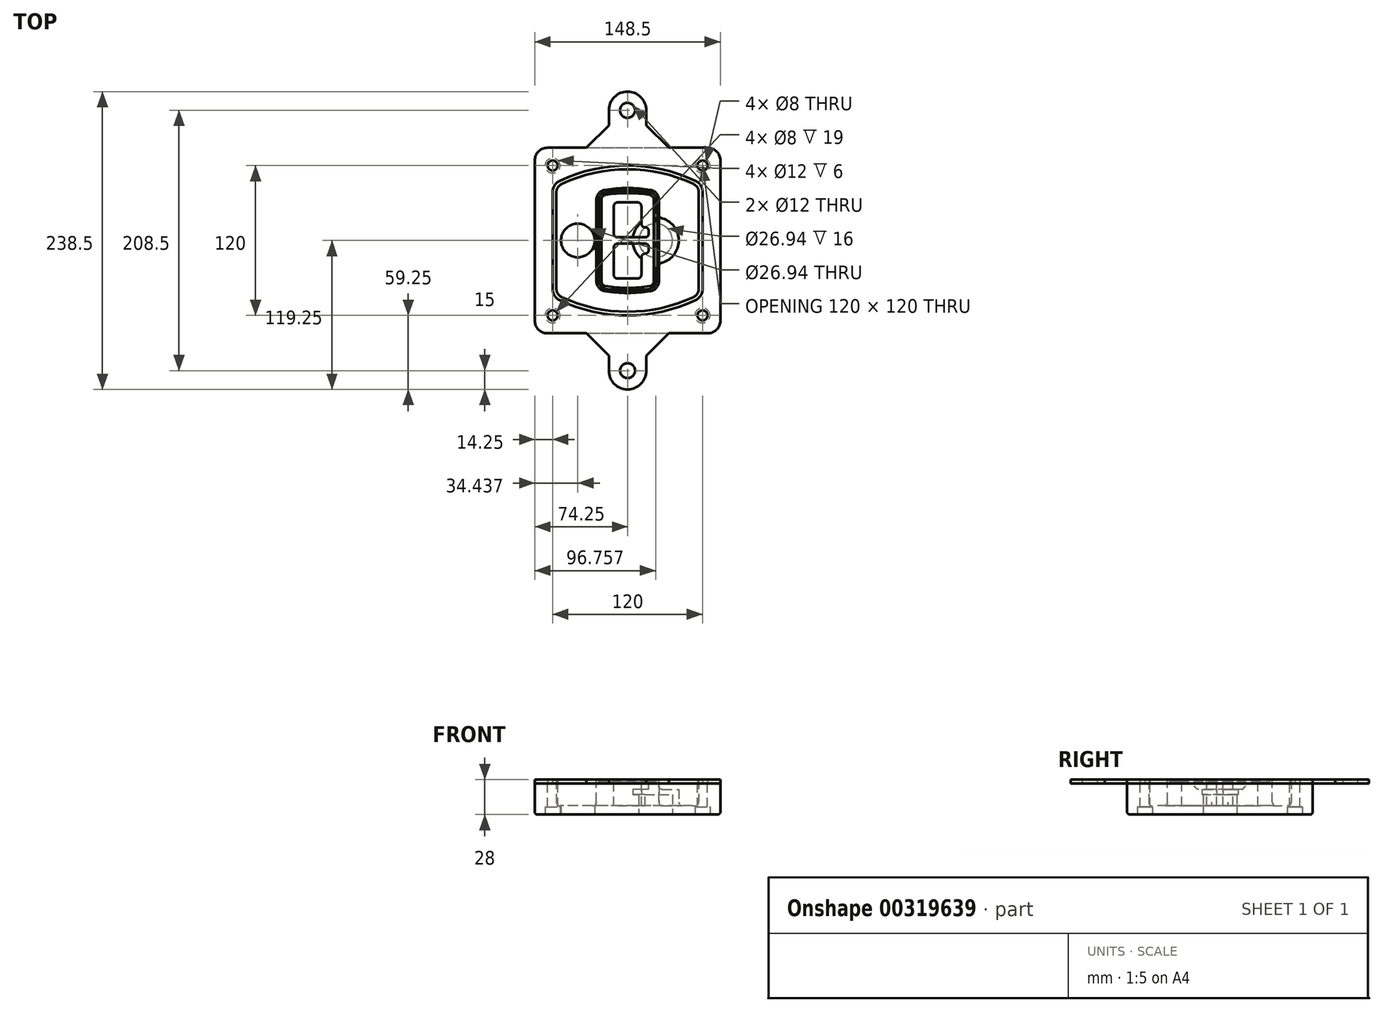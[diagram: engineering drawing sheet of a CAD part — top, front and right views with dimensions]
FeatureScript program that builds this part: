
annotation { "Feature Type Name" : "Feature", "Feature Type Description" : "" }
export const myFeature = defineFeature(function(context is Context, id is Id, definition is map)
    precondition{}
    {
        {
            var Q0;
            Q0=qCreatedBy(makeId("Top.planeOp"),FACE);
            var sketch = newSketch(context, id + "F0", { "sketchPlane" : qUnion([Q0])});
            skPoint(sketch, "E0.rect.middle", {"position": v(0, 0) * mm});
            skLineSegment(sketch, "E1.bottom", {"start": v(-64.25, -74.25) * mm, "end": v(64.25, -74.25) * mm});
            skLineSegment(sketch, "E1.top", {"start": v(-64.25, 74.25) * mm, "end": v(64.25, 74.25) * mm});
            skLineSegment(sketch, "E1.left", {"start": v(-74.25, -64.25) * mm, "end": v(-74.25, 64.25) * mm});
            skLineSegment(sketch, "E1.right", {"start": v(74.25, -64.25) * mm, "end": v(74.25, 64.25) * mm});
            skLineSegment(sketch, "E2", {"start": v(-74.25, 74.25) * mm, "end": v(74.25, -74.25) * mm, "construction": true});
            skLineSegment(sketch, "E3", {"start": v(74.25, 74.25) * mm, "end": v(-74.25, -74.25) * mm, "construction": true});
            skCircle(sketch, "E4", {"center": v(-60, 60) * mm, "radius": 4 * mm});
            skCircle(sketch, "E5", {"center": v(60, 60) * mm, "radius": 4 * mm});
            skCircle(sketch, "E6", {"center": v(60, -60) * mm, "radius": 4 * mm});
            skCircle(sketch, "E7", {"center": v(-60, -60) * mm, "radius": 4 * mm});
            skLineSegment(sketch, "E8", {"start": v(-60, 60) * mm, "end": v(60, 60) * mm, "construction": true});
            skLineSegment(sketch, "E9", {"start": v(60, 60) * mm, "end": v(60, -60) * mm, "construction": true});
            skLineSegment(sketch, "E10", {"start": v(60, -60) * mm, "end": v(-60, -60) * mm, "construction": true});
            skLineSegment(sketch, "E11", {"start": v(-60, -60) * mm, "end": v(-60, 60) * mm, "construction": true});
            skLineSegment(sketch, "E12", {"start": v(-60, 38.83) * mm, "end": v(-60, -38.83) * mm});
            skLineSegment(sketch, "E13", {"start": v(60, 38.83) * mm, "end": v(60, -38.83) * mm});
            skArc(sketch, "E14", {"start": v(54.26, 47.88) * mm, "mid": v(0, 60) * mm, "end": v(-54.26, 47.88) * mm});
            skArc(sketch, "E15", {"start": v(-54.26, -47.88) * mm, "mid": v(0, -60) * mm, "end": v(54.26, -47.88) * mm});
            skLineSegment(sketch, "E16", {"start": v(-60, 0) * mm, "end": v(60, 0) * mm, "construction": true});
            skPoint(sketch, "E17.visualSharp", {"position": v(-60, -45) * mm});
            skArc(sketch, "E17.filletArc", {"start": v(-60, -38.83) * mm, "mid": v(-58.44, -44.2) * mm, "end": v(-54.26, -47.88) * mm});
            skPoint(sketch, "E18.visualSharp", {"position": v(-60, 45) * mm});
            skArc(sketch, "E18.filletArc", {"start": v(-54.26, 47.88) * mm, "mid": v(-58.44, 44.2) * mm, "end": v(-60, 38.83) * mm});
            skPoint(sketch, "E19.visualSharp", {"position": v(60, 45) * mm});
            skArc(sketch, "E19.filletArc", {"start": v(60, 38.83) * mm, "mid": v(58.44, 44.2) * mm, "end": v(54.26, 47.88) * mm});
            skPoint(sketch, "E20.visualSharp", {"position": v(60, -45) * mm});
            skArc(sketch, "E20.filletArc", {"start": v(54.26, -47.88) * mm, "mid": v(58.44, -44.2) * mm, "end": v(60, -38.83) * mm});
            skPoint(sketch, "E21.visualSharp", {"position": v(-74.25, 74.25) * mm});
            skArc(sketch, "E21.filletArc", {"start": v(-64.25, 74.25) * mm, "mid": v(-71.32, 71.32) * mm, "end": v(-74.25, 64.25) * mm});
            skPoint(sketch, "E22.visualSharp", {"position": v(74.25, 74.25) * mm});
            skArc(sketch, "E22.filletArc", {"start": v(74.25, 64.25) * mm, "mid": v(71.32, 71.32) * mm, "end": v(64.25, 74.25) * mm});
            skPoint(sketch, "E23.visualSharp", {"position": v(74.25, -74.25) * mm});
            skArc(sketch, "E23.filletArc", {"start": v(64.25, -74.25) * mm, "mid": v(71.32, -71.32) * mm, "end": v(74.25, -64.25) * mm});
            skPoint(sketch, "E24.visualSharp", {"position": v(-74.25, -74.25) * mm});
            skArc(sketch, "E24.filletArc", {"start": v(-74.25, -64.25) * mm, "mid": v(-71.32, -71.32) * mm, "end": v(-64.25, -74.25) * mm});
            skArc(sketch, "E25.0", {"start": v(57, 38.83) * mm, "mid": v(55.9, 42.58) * mm, "end": v(52.98, 45.17) * mm});
            skLineSegment(sketch, "E25.1", {"start": v(57, 38.83) * mm, "end": v(57, -38.83) * mm});
            skArc(sketch, "E25.2", {"start": v(52.98, -45.17) * mm, "mid": v(55.9, -42.58) * mm, "end": v(57, -38.83) * mm});
            skArc(sketch, "E25.3", {"start": v(-52.98, -45.17) * mm, "mid": v(0, -57) * mm, "end": v(52.98, -45.17) * mm});
            skArc(sketch, "E25.4", {"start": v(-57, -38.83) * mm, "mid": v(-55.9, -42.58) * mm, "end": v(-52.98, -45.17) * mm});
            skArc(sketch, "E25.5", {"start": v(52.98, 45.17) * mm, "mid": v(0, 57) * mm, "end": v(-52.98, 45.17) * mm});
            skLineSegment(sketch, "E25.6", {"start": v(-57, 38.83) * mm, "end": v(-57, -38.83) * mm});
            skArc(sketch, "E25.7", {"start": v(-52.98, 45.17) * mm, "mid": v(-55.9, 42.58) * mm, "end": v(-57, 38.83) * mm});
            skArc(sketch, "E26.0", {"start": v(-55.96, 51.5) * mm, "mid": v(-61.82, 46.33) * mm, "end": v(-64, 38.83) * mm});
            skArc(sketch, "E26.1", {"start": v(55.96, 51.5) * mm, "mid": v(0, 64) * mm, "end": v(-55.96, 51.5) * mm});
            skArc(sketch, "E26.2", {"start": v(64, 38.83) * mm, "mid": v(61.82, 46.33) * mm, "end": v(55.96, 51.5) * mm});
            skLineSegment(sketch, "E26.3", {"start": v(64, 38.83) * mm, "end": v(64, -38.83) * mm});
            skArc(sketch, "E26.4", {"start": v(55.96, -51.5) * mm, "mid": v(61.82, -46.33) * mm, "end": v(64, -38.83) * mm});
            skLineSegment(sketch, "E26.5", {"start": v(-64, 38.83) * mm, "end": v(-64, -38.83) * mm});
            skArc(sketch, "E26.6", {"start": v(-55.96, -51.5) * mm, "mid": v(0, -64) * mm, "end": v(55.96, -51.5) * mm});
            skArc(sketch, "E26.7", {"start": v(-64, -38.83) * mm, "mid": v(-61.82, -46.33) * mm, "end": v(-55.96, -51.5) * mm});
            skSolve(sketch);
        }
        {
            var Q0;
            Q0=makeQuery(id+"F0.imprint","IMPRINT",FACE,{"disambiguationData":[TD([[makeQuery(id+"F0.imprint","IMPRINT",EDGE,{"derivedFrom":sQuery(id+"F0.wireOp",EDGE,"E1.bottom")}),1.0]])]});
            var Q1;
            Q1=makeQuery(id+"F0.imprint","IMPRINT",FACE,{"disambiguationData":[TD([[makeQuery(id+"F0.imprint","IMPRINT",EDGE,{"derivedFrom":sQuery(id+"F0.wireOp",EDGE,"E12")}),1.0]])]});
            var Q2;
            Q2=makeQuery(id+"F0.imprint","IMPRINT",FACE,{"disambiguationData":[TD([[makeQuery(id+"F0.imprint","IMPRINT",EDGE,{"derivedFrom":sQuery(id+"F0.wireOp",EDGE,"E25.0")}),1.0]])]});
            var Q3;
            Q3=makeQuery(id+"F0.imprint","IMPRINT",FACE,{"disambiguationData":[TD([[makeQuery(id+"F0.imprint","IMPRINT",EDGE,{"derivedFrom":sQuery(id+"F0.wireOp",EDGE,"E12")}),-1.0]])]});
            extrude(context, id + "F1", {"entities" : qUnion([Q0, Q1, Q2, Q3]), "oppositeDirection" : true, "depth" : 25 * mm});
        }
        {
            var Q0;
            Q0=makeQuery(id+"F0.imprint","IMPRINT",FACE,{"disambiguationData":[TD([[makeQuery(id+"F0.imprint","IMPRINT",EDGE,{"derivedFrom":sQuery(id+"F0.wireOp",EDGE,"E12")}),1.0]])]});
            extrude(context, id + "F2", {"entities" : qUnion([Q0]), "operationType" : NewBodyOperationType.ADD, "depth" : 3 * mm});
        }
        {
            var Q0;
            Q0=makeQuery(id+"F0.imprint","IMPRINT",FACE,{"disambiguationData":[TD([[makeQuery(id+"F0.imprint","IMPRINT",EDGE,{"derivedFrom":sQuery(id+"F0.wireOp",EDGE,"E25.0")}),1.0]])]});
            extrude(context, id + "F3", {"entities" : qUnion([Q0]), "operationType" : NewBodyOperationType.REMOVE, "oppositeDirection" : true, "depth" : 18 * mm});
        }
        {
            var Q0;
            Q0=makeQuery(id+"F2.opExtrude","CAP_FACE",FACE,{"disambiguationData":[OSD([sQuery(id+"F0.wireOp",EDGE,"E12"),sQuery(id+"F0.wireOp",EDGE,"E13"),sQuery(id+"F0.wireOp",EDGE,"E14"),sQuery(id+"F0.wireOp",EDGE,"E15"),sQuery(id+"F0.wireOp",EDGE,"E17.filletArc"),sQuery(id+"F0.wireOp",EDGE,"E18.filletArc"),sQuery(id+"F0.wireOp",EDGE,"E19.filletArc"),sQuery(id+"F0.wireOp",EDGE,"E20.filletArc"),sQuery(id+"F0.wireOp",EDGE,"E25.0"),sQuery(id+"F0.wireOp",EDGE,"E25.1"),sQuery(id+"F0.wireOp",EDGE,"E25.2"),sQuery(id+"F0.wireOp",EDGE,"E25.3"),sQuery(id+"F0.wireOp",EDGE,"E25.4"),sQuery(id+"F0.wireOp",EDGE,"E25.5"),sQuery(id+"F0.wireOp",EDGE,"E25.6"),sQuery(id+"F0.wireOp",EDGE,"E25.7")])],"isStart":false});
            var sketch = newSketch(context, id + "F4", { "sketchPlane" : qUnion([Q0])});
            skArc(sketch, "E27.0", {"start": v(-18.34, -40.45) * mm, "mid": v(0, -42) * mm, "end": v(18.34, -40.45) * mm});
            skArc(sketch, "E28.0", {"start": v(18.34, 40.45) * mm, "mid": v(0, 42) * mm, "end": v(-18.34, 40.45) * mm});
            skLineSegment(sketch, "E29", {"start": v(-25, 32.57) * mm, "end": v(-25, -32.57) * mm});
            skLineSegment(sketch, "E30", {"start": v(25, 32.57) * mm, "end": v(25, -32.57) * mm});
            skLineSegment(sketch, "E31", {"start": v(-25, 39.1) * mm, "end": v(25, 39.1) * mm, "construction": true});
            skLineSegment(sketch, "E32", {"start": v(-25, -39.1) * mm, "end": v(25, -39.1) * mm, "construction": true});
            skPoint(sketch, "E33.visualSharp", {"position": v(-25, 39.1) * mm});
            skArc(sketch, "E33.filletArc", {"start": v(-18.34, 40.45) * mm, "mid": v(-23.11, 37.73) * mm, "end": v(-25, 32.57) * mm});
            skPoint(sketch, "E34.visualSharp", {"position": v(25, 39.1) * mm});
            skArc(sketch, "E34.filletArc", {"start": v(25, 32.57) * mm, "mid": v(23.11, 37.73) * mm, "end": v(18.34, 40.45) * mm});
            skPoint(sketch, "E35.visualSharp", {"position": v(25, -39.1) * mm});
            skArc(sketch, "E35.filletArc", {"start": v(18.34, -40.45) * mm, "mid": v(23.11, -37.73) * mm, "end": v(25, -32.57) * mm});
            skPoint(sketch, "E36.visualSharp", {"position": v(-25, -39.1) * mm});
            skArc(sketch, "E36.filletArc", {"start": v(-25, -32.57) * mm, "mid": v(-23.11, -37.73) * mm, "end": v(-18.34, -40.45) * mm});
            skArc(sketch, "E37.0", {"start": v(52.98, 45.17) * mm, "mid": v(0, 57) * mm, "end": v(-52.98, 45.17) * mm});
            skArc(sketch, "E37.1", {"start": v(-52.98, 45.17) * mm, "mid": v(-55.9, 42.58) * mm, "end": v(-57, 38.83) * mm});
            skLineSegment(sketch, "E37.2", {"start": v(-57, 38.83) * mm, "end": v(-57, -38.83) * mm});
            skArc(sketch, "E37.3", {"start": v(-57, -38.83) * mm, "mid": v(-55.9, -42.58) * mm, "end": v(-52.98, -45.17) * mm});
            skArc(sketch, "E37.4", {"start": v(-52.98, -45.17) * mm, "mid": v(0, -57) * mm, "end": v(52.98, -45.17) * mm});
            skArc(sketch, "E37.5", {"start": v(52.98, -45.17) * mm, "mid": v(55.9, -42.58) * mm, "end": v(57, -38.83) * mm});
            skLineSegment(sketch, "E37.6", {"start": v(57, 38.83) * mm, "end": v(57, -38.83) * mm});
            skArc(sketch, "E37.7", {"start": v(57, 38.83) * mm, "mid": v(55.9, 42.58) * mm, "end": v(52.98, 45.17) * mm});
            skLineSegment(sketch, "E38.0", {"start": v(23, 32.57) * mm, "end": v(23, -32.57) * mm});
            skArc(sketch, "E38.1", {"start": v(18, -38.48) * mm, "mid": v(21.58, -36.44) * mm, "end": v(23, -32.57) * mm});
            skArc(sketch, "E38.2", {"start": v(-18, -38.48) * mm, "mid": v(0, -40) * mm, "end": v(18, -38.48) * mm});
            skArc(sketch, "E38.3", {"start": v(-23, -32.57) * mm, "mid": v(-21.58, -36.44) * mm, "end": v(-18, -38.48) * mm});
            skLineSegment(sketch, "E38.4", {"start": v(-23, 32.57) * mm, "end": v(-23, -32.57) * mm});
            skArc(sketch, "E38.5", {"start": v(23, 32.57) * mm, "mid": v(21.58, 36.44) * mm, "end": v(18, 38.48) * mm});
            skArc(sketch, "E38.6", {"start": v(-18, 38.48) * mm, "mid": v(-21.58, 36.44) * mm, "end": v(-23, 32.57) * mm});
            skArc(sketch, "E38.7", {"start": v(18, 38.48) * mm, "mid": v(0, 40) * mm, "end": v(-18, 38.48) * mm});
            skArc(sketch, "E39.0", {"start": v(21, 32.57) * mm, "mid": v(20.06, 35.15) * mm, "end": v(17.67, 36.5) * mm});
            skLineSegment(sketch, "E39.1", {"start": v(21, 32.57) * mm, "end": v(21, -32.57) * mm});
            skArc(sketch, "E39.2", {"start": v(17.67, -36.5) * mm, "mid": v(20.06, -35.15) * mm, "end": v(21, -32.57) * mm});
            skArc(sketch, "E39.3", {"start": v(-17.67, -36.5) * mm, "mid": v(0, -38) * mm, "end": v(17.67, -36.5) * mm});
            skArc(sketch, "E39.4", {"start": v(-21, -32.57) * mm, "mid": v(-20.06, -35.15) * mm, "end": v(-17.67, -36.5) * mm});
            skArc(sketch, "E39.5", {"start": v(17.67, 36.5) * mm, "mid": v(0, 38) * mm, "end": v(-17.67, 36.5) * mm});
            skLineSegment(sketch, "E39.6", {"start": v(-21, 32.57) * mm, "end": v(-21, -32.57) * mm});
            skArc(sketch, "E39.7", {"start": v(-17.67, 36.5) * mm, "mid": v(-20.06, 35.15) * mm, "end": v(-21, 32.57) * mm});
            skLineSegment(sketch, "E40", {"start": v(-25, 0) * mm, "end": v(25, 0) * mm, "construction": true});
            skLineSegment(sketch, "E41", {"start": v(-11, 5.5) * mm, "end": v(-11, 27.5) * mm});
            skLineSegment(sketch, "E42", {"start": v(-8, 30.5) * mm, "end": v(8, 30.5) * mm});
            skLineSegment(sketch, "E43", {"start": v(11, 27.5) * mm, "end": v(11, 13.5) * mm});
            skLineSegment(sketch, "E44", {"start": v(14, 10.5) * mm, "end": v(14, 10.5) * mm});
            skLineSegment(sketch, "E45", {"start": v(17, 7.5) * mm, "end": v(17, 5.5) * mm});
            skLineSegment(sketch, "E46", {"start": v(14, 2.5) * mm, "end": v(-8, 2.5) * mm});
            skPoint(sketch, "E47.visualSharp", {"position": v(-11, 30.5) * mm});
            skArc(sketch, "E47.filletArc", {"start": v(-8, 30.5) * mm, "mid": v(-10.12, 29.62) * mm, "end": v(-11, 27.5) * mm});
            skPoint(sketch, "E48.visualSharp", {"position": v(11, 30.5) * mm});
            skArc(sketch, "E48.filletArc", {"start": v(11, 27.5) * mm, "mid": v(10.12, 29.62) * mm, "end": v(8, 30.5) * mm});
            skPoint(sketch, "E49.visualSharp", {"position": v(11, 10.5) * mm});
            skArc(sketch, "E49.filletArc", {"start": v(11, 13.5) * mm, "mid": v(11.88, 11.38) * mm, "end": v(14, 10.5) * mm});
            skPoint(sketch, "E50.visualSharp", {"position": v(17, 10.5) * mm});
            skArc(sketch, "E50.filletArc", {"start": v(17, 7.5) * mm, "mid": v(16.12, 9.62) * mm, "end": v(14, 10.5) * mm});
            skPoint(sketch, "E51.visualSharp", {"position": v(17, 2.5) * mm});
            skArc(sketch, "E51.filletArc", {"start": v(14, 2.5) * mm, "mid": v(16.12, 3.38) * mm, "end": v(17, 5.5) * mm});
            skPoint(sketch, "E52.visualSharp", {"position": v(-11, 2.5) * mm});
            skArc(sketch, "E52.filletArc", {"start": v(-11, 5.5) * mm, "mid": v(-10.12, 3.38) * mm, "end": v(-8, 2.5) * mm});
            skLineSegment(sketch, "E53.0.MirrorCS", {"start": v(14, -2.5) * mm, "end": v(-8, -2.5) * mm});
            skArc(sketch, "E54.0.MirrorCS", {"start": v(-11, -5.5) * mm, "mid": v(-10.12, -3.38) * mm, "end": v(-8, -2.5) * mm});
            skLineSegment(sketch, "E55.0.MirrorCS", {"start": v(-11, -5.5) * mm, "end": v(-11, -27.5) * mm});
            skArc(sketch, "E56.0.MirrorCS", {"start": v(-8, -30.5) * mm, "mid": v(-10.12, -29.62) * mm, "end": v(-11, -27.5) * mm});
            skLineSegment(sketch, "E57.0.MirrorCS", {"start": v(-8, -30.5) * mm, "end": v(8, -30.5) * mm});
            skArc(sketch, "E58.0.MirrorCS", {"start": v(11, -27.5) * mm, "mid": v(10.12, -29.62) * mm, "end": v(8, -30.5) * mm});
            skLineSegment(sketch, "E59.0.MirrorCS", {"start": v(11, -27.5) * mm, "end": v(11, -13.5) * mm});
            skArc(sketch, "E60.0.MirrorCS", {"start": v(11, -13.5) * mm, "mid": v(11.88, -11.38) * mm, "end": v(14, -10.5) * mm});
            skArc(sketch, "E61.0.MirrorCS", {"start": v(17, -7.5) * mm, "mid": v(16.12, -9.62) * mm, "end": v(14, -10.5) * mm});
            skLineSegment(sketch, "E62.0.MirrorCS", {"start": v(17, -7.5) * mm, "end": v(17, -5.5) * mm});
            skArc(sketch, "E63.0.MirrorCS", {"start": v(14, -2.5) * mm, "mid": v(16.12, -3.38) * mm, "end": v(17, -5.5) * mm});
            skSolve(sketch);
        }
        {
            var Q0;
            Q0=makeQuery(id+"F4.imprint","IMPRINT",FACE,{"disambiguationData":[TD([[makeQuery(id+"F4.imprint","IMPRINT",EDGE,{"derivedFrom":sQuery(id+"F4.wireOp",EDGE,"E27.0")}),1.0]])]});
            var Q1;
            Q1=makeQuery(id+"F4.imprint","IMPRINT",FACE,{"disambiguationData":[TD([[makeQuery(id+"F4.imprint","IMPRINT",EDGE,{"derivedFrom":sQuery(id+"F4.wireOp",EDGE,"E38.0")}),-1.0]])]});
            var Q2;
            Q2=makeQuery(id+"F4.imprint","IMPRINT",FACE,{"disambiguationData":[TD([[makeQuery(id+"F4.imprint","IMPRINT",EDGE,{"derivedFrom":sQuery(id+"F4.wireOp",EDGE,"E39.0")}),1.0]])]});
            extrude(context, id + "F5", {"entities" : qUnion([Q0, Q1, Q2]), "operationType" : NewBodyOperationType.ADD, "endBound" : BoundingType.UP_TO_NEXT, "oppositeDirection" : true, "depth" : 25 * mm});
        }
        {
            var Q0;
            Q0=makeQuery(id+"F4.imprint","IMPRINT",FACE,{"disambiguationData":[TD([[makeQuery(id+"F4.imprint","IMPRINT",EDGE,{"derivedFrom":sQuery(id+"F4.wireOp",EDGE,"E38.0")}),-1.0]])]});
            extrude(context, id + "F6", {"entities" : qUnion([Q0]), "operationType" : NewBodyOperationType.REMOVE, "oppositeDirection" : true, "depth" : 2 * mm});
        }
        {
            var Q0;
            Q0=makeQuery(id+"F1.opExtrude","CAP_FACE",FACE,{"disambiguationData":[OSD([sQuery(id+"F0.wireOp",EDGE,"E1.bottom"),sQuery(id+"F0.wireOp",EDGE,"E1.top"),sQuery(id+"F0.wireOp",EDGE,"E1.left"),sQuery(id+"F0.wireOp",EDGE,"E1.right"),sQuery(id+"F0.wireOp",EDGE,"E4"),sQuery(id+"F0.wireOp",EDGE,"E5"),sQuery(id+"F0.wireOp",EDGE,"E6"),sQuery(id+"F0.wireOp",EDGE,"E7"),sQuery(id+"F0.wireOp",EDGE,"E21.filletArc"),sQuery(id+"F0.wireOp",EDGE,"E22.filletArc"),sQuery(id+"F0.wireOp",EDGE,"E23.filletArc"),sQuery(id+"F0.wireOp",EDGE,"E24.filletArc")])],"isStart":false});
            var sketch = newSketch(context, id + "F7", { "sketchPlane" : qUnion([Q0])});
            skCircle(sketch, "E64", {"center": v(22.5, 0) * mm, "radius": 13.47 * mm});
            skCircle(sketch, "E65", {"center": v(-39.81, 0) * mm, "radius": 13.47 * mm});
            skLineSegment(sketch, "E66", {"start": v(74.25, 0) * mm, "end": v(-74.25, 0) * mm});
            skCircle(sketch, "E67", {"center": v(22.5, 0) * mm, "radius": 18.47 * mm});
            skCircle(sketch, "E68", {"center": v(60, -60) * mm, "radius": 6 * mm});
            skCircle(sketch, "E69", {"center": v(-60, -60) * mm, "radius": 6 * mm});
            skCircle(sketch, "E70", {"center": v(-60, 60) * mm, "radius": 6 * mm});
            skCircle(sketch, "E71", {"center": v(60, 60) * mm, "radius": 6 * mm});
            skSolve(sketch);
        }
        {
            var Q0;
            {var subQ1=sQuery(id+"F7.wireOp",EDGE,"E66");var subQ4=sQuery(id+"F7.wireOp",EDGE,"E64");var subQ6=makeQuery(id+"F7.imprint","INTERSECT",VERTEX,{"disambiguationData":[OD(0.0)],"derivedFrom":[subQ4,subQ1]});Q0=makeQuery(id+"F7.imprint","IMPRINT",FACE,{"disambiguationData":[TD([[makeQuery(id+"F7.imprint","IMPRINT",EDGE,{"disambiguationData":[TD([[subQ6,-1.0]])],"derivedFrom":subQ4}),-1.0]])]});}
            var Q1;
            {var subQ0=sQuery(id+"F7.wireOp",EDGE,"E66");var subQ1=sQuery(id+"F7.wireOp",EDGE,"E64");var subQ3=makeQuery(id+"F7.imprint","INTERSECT",VERTEX,{"disambiguationData":[OD(0.0)],"derivedFrom":[subQ1,subQ0]});Q1=makeQuery(id+"F7.imprint","IMPRINT",FACE,{"disambiguationData":[TD([[makeQuery(id+"F7.imprint","IMPRINT",EDGE,{"disambiguationData":[TD([[subQ3,-1.0]])],"derivedFrom":subQ1}),1.0]])]});}
            var Q2;
            {var subQ0=sQuery(id+"F7.wireOp",EDGE,"E66");var subQ1=sQuery(id+"F7.wireOp",EDGE,"E64");var subQ3=makeQuery(id+"F7.imprint","INTERSECT",VERTEX,{"disambiguationData":[OD(0.0)],"derivedFrom":[subQ1,subQ0]});Q2=makeQuery(id+"F7.imprint","IMPRINT",FACE,{"disambiguationData":[TD([[makeQuery(id+"F7.imprint","IMPRINT",EDGE,{"disambiguationData":[TD([[subQ3,1.0]])],"derivedFrom":subQ1}),1.0]])]});}
            var Q3;
            {var subQ1=sQuery(id+"F7.wireOp",EDGE,"E66");var subQ4=sQuery(id+"F7.wireOp",EDGE,"E64");var subQ6=makeQuery(id+"F7.imprint","INTERSECT",VERTEX,{"disambiguationData":[OD(0.0)],"derivedFrom":[subQ4,subQ1]});Q3=makeQuery(id+"F7.imprint","IMPRINT",FACE,{"disambiguationData":[TD([[makeQuery(id+"F7.imprint","IMPRINT",EDGE,{"disambiguationData":[TD([[subQ6,1.0]])],"derivedFrom":subQ4}),-1.0]])]});}
            extrude(context, id + "F8", {"entities" : qUnion([Q0, Q1, Q2, Q3]), "operationType" : NewBodyOperationType.ADD, "oppositeDirection" : true, "depth" : 20 * mm});
        }
        {
            var Q0;
            {var subQ0=sQuery(id+"F7.wireOp",EDGE,"E66");var subQ1=sQuery(id+"F7.wireOp",EDGE,"E64");var subQ3=makeQuery(id+"F7.imprint","INTERSECT",VERTEX,{"disambiguationData":[OD(0.0)],"derivedFrom":[subQ1,subQ0]});Q0=makeQuery(id+"F7.imprint","IMPRINT",FACE,{"disambiguationData":[TD([[makeQuery(id+"F7.imprint","IMPRINT",EDGE,{"disambiguationData":[TD([[subQ3,-1.0]])],"derivedFrom":subQ1}),1.0]])]});}
            var Q1;
            {var subQ0=sQuery(id+"F7.wireOp",EDGE,"E66");var subQ1=sQuery(id+"F7.wireOp",EDGE,"E64");var subQ3=makeQuery(id+"F7.imprint","INTERSECT",VERTEX,{"disambiguationData":[OD(0.0)],"derivedFrom":[subQ1,subQ0]});Q1=makeQuery(id+"F7.imprint","IMPRINT",FACE,{"disambiguationData":[TD([[makeQuery(id+"F7.imprint","IMPRINT",EDGE,{"disambiguationData":[TD([[subQ3,1.0]])],"derivedFrom":subQ1}),1.0]])]});}
            extrude(context, id + "F9", {"entities" : qUnion([Q0, Q1]), "operationType" : NewBodyOperationType.REMOVE, "oppositeDirection" : true, "depth" : 16 * mm});
        }
        {
            var Q0;
            {var subQ0=sQuery(id+"F7.wireOp",EDGE,"E66");var subQ1=sQuery(id+"F7.wireOp",EDGE,"E65");var subQ3=makeQuery(id+"F7.imprint","INTERSECT",VERTEX,{"disambiguationData":[OD(0.0)],"derivedFrom":[subQ1,subQ0]});Q0=makeQuery(id+"F7.imprint","IMPRINT",FACE,{"disambiguationData":[TD([[makeQuery(id+"F7.imprint","IMPRINT",EDGE,{"disambiguationData":[TD([[subQ3,-1.0]])],"derivedFrom":subQ1}),1.0]])]});}
            var Q1;
            {var subQ0=sQuery(id+"F7.wireOp",EDGE,"E66");var subQ1=sQuery(id+"F7.wireOp",EDGE,"E65");var subQ3=makeQuery(id+"F7.imprint","INTERSECT",VERTEX,{"disambiguationData":[OD(0.0)],"derivedFrom":[subQ1,subQ0]});Q1=makeQuery(id+"F7.imprint","IMPRINT",FACE,{"disambiguationData":[TD([[makeQuery(id+"F7.imprint","IMPRINT",EDGE,{"disambiguationData":[TD([[subQ3,1.0]])],"derivedFrom":subQ1}),1.0]])]});}
            extrude(context, id + "F10", {"entities" : qUnion([Q0, Q1]), "operationType" : NewBodyOperationType.REMOVE, "oppositeDirection" : true, "depth" : 25 * mm});
        }
        {
            var Q0;
            Q0=makeQuery(id+"F7.imprint","IMPRINT",FACE,{"disambiguationData":[TD([[makeQuery(id+"F7.imprint","IMPRINT",EDGE,{"derivedFrom":sQuery(id+"F7.wireOp",EDGE,"E68")}),1.0]])]});
            var Q1;
            Q1=makeQuery(id+"F7.imprint","IMPRINT",FACE,{"disambiguationData":[TD([[makeQuery(id+"F7.imprint","IMPRINT",EDGE,{"derivedFrom":makeQuery(id+"F1.opExtrude","CAP_EDGE",EDGE,{"disambiguationData":[OSD([sQuery(id+"F0.wireOp",EDGE,"E5")])],"isStart":false})}),-1.0]])]});
            var Q2;
            Q2=makeQuery(id+"F7.imprint","IMPRINT",FACE,{"disambiguationData":[TD([[makeQuery(id+"F7.imprint","IMPRINT",EDGE,{"derivedFrom":sQuery(id+"F7.wireOp",EDGE,"E69")}),1.0]])]});
            var Q3;
            Q3=makeQuery(id+"F7.imprint","IMPRINT",FACE,{"disambiguationData":[TD([[makeQuery(id+"F7.imprint","IMPRINT",EDGE,{"derivedFrom":makeQuery(id+"F1.opExtrude","CAP_EDGE",EDGE,{"disambiguationData":[OSD([sQuery(id+"F0.wireOp",EDGE,"E4")])],"isStart":false})}),-1.0]])]});
            var Q4;
            Q4=makeQuery(id+"F7.imprint","IMPRINT",FACE,{"disambiguationData":[TD([[makeQuery(id+"F7.imprint","IMPRINT",EDGE,{"derivedFrom":sQuery(id+"F7.wireOp",EDGE,"E70")}),1.0]])]});
            var Q5;
            Q5=makeQuery(id+"F7.imprint","IMPRINT",FACE,{"disambiguationData":[TD([[makeQuery(id+"F7.imprint","IMPRINT",EDGE,{"derivedFrom":makeQuery(id+"F1.opExtrude","CAP_EDGE",EDGE,{"disambiguationData":[OSD([sQuery(id+"F0.wireOp",EDGE,"E7")])],"isStart":false})}),-1.0]])]});
            var Q6;
            Q6=makeQuery(id+"F7.imprint","IMPRINT",FACE,{"disambiguationData":[TD([[makeQuery(id+"F7.imprint","IMPRINT",EDGE,{"derivedFrom":sQuery(id+"F7.wireOp",EDGE,"E71")}),1.0]])]});
            var Q7;
            Q7=makeQuery(id+"F7.imprint","IMPRINT",FACE,{"disambiguationData":[TD([[makeQuery(id+"F7.imprint","IMPRINT",EDGE,{"derivedFrom":makeQuery(id+"F1.opExtrude","CAP_EDGE",EDGE,{"disambiguationData":[OSD([sQuery(id+"F0.wireOp",EDGE,"E6")])],"isStart":false})}),-1.0]])]});
            extrude(context, id + "F11", {"entities" : qUnion([Q0, Q1, Q2, Q3, Q4, Q5, Q6, Q7]), "operationType" : NewBodyOperationType.REMOVE, "oppositeDirection" : true, "depth" : 6 * mm});
        }
        {
            var Q0;
            Q0=makeQuery(id+"F9.boolean.opBoolean","COPY",FACE,{"derivedFrom":makeQuery(id+"F9.opExtrude","CAP_FACE",FACE,{"disambiguationData":[OSD([sQuery(id+"F7.wireOp",EDGE,"E64")])],"isStart":false})});
            var sketch = newSketch(context, id + "F12", { "sketchPlane" : qUnion([Q0])});
            skArc(sketch, "E72.0", {"start": v(11, 14.45) * mm, "mid": v(6.45, 9.13) * mm, "end": v(4.2, 2.5) * mm});
            skArc(sketch, "E72.1", {"start": v(4.2, -2.5) * mm, "mid": v(6.45, -9.13) * mm, "end": v(11, -14.45) * mm});
            skLineSegment(sketch, "E73", {"start": v(4.2, -2.5) * mm, "end": v(14, -2.5) * mm});
            skLineSegment(sketch, "E74.0", {"start": v(14, 2.5) * mm, "end": v(4.2, 2.5) * mm});
            skArc(sketch, "E74.1", {"start": v(14, 2.5) * mm, "mid": v(16.12, 3.38) * mm, "end": v(17, 5.5) * mm});
            skLineSegment(sketch, "E74.2", {"start": v(17, 7.5) * mm, "end": v(17, 5.5) * mm});
            skArc(sketch, "E74.3", {"start": v(17, 7.5) * mm, "mid": v(16.12, 9.62) * mm, "end": v(14, 10.5) * mm});
            skArc(sketch, "E74.4", {"start": v(11, 13.5) * mm, "mid": v(11.88, 11.38) * mm, "end": v(14, 10.5) * mm});
            skLineSegment(sketch, "E74.5", {"start": v(11, 14.45) * mm, "end": v(11, 13.5) * mm});
            skLineSegment(sketch, "E74.7", {"start": v(14, -2.5) * mm, "end": v(4.2, -2.5) * mm});
            skArc(sketch, "E74.8", {"start": v(14, -2.5) * mm, "mid": v(16.12, -3.38) * mm, "end": v(17, -5.5) * mm});
            skLineSegment(sketch, "E74.9", {"start": v(17, -7.5) * mm, "end": v(17, -5.5) * mm});
            skArc(sketch, "E74.10", {"start": v(17, -7.5) * mm, "mid": v(16.12, -9.62) * mm, "end": v(14, -10.5) * mm});
            skArc(sketch, "E74.11", {"start": v(11, -13.5) * mm, "mid": v(11.88, -11.38) * mm, "end": v(14, -10.5) * mm});
            skLineSegment(sketch, "E74.12", {"start": v(11, -14.45) * mm, "end": v(11, -13.5) * mm});
            skPoint(sketch, "E75.orphan", {"position": v(11, -27.5) * mm});
            skPoint(sketch, "E76.orphan", {"position": v(-8, -2.5) * mm});
            skPoint(sketch, "E77.orphan", {"position": v(-8, 2.5) * mm});
            skPoint(sketch, "E78.orphan", {"position": v(11, 27.5) * mm});
            skSolve(sketch);
        }
        {
            var Q0;
            {var subQ7=sQuery(id+"F12.wireOp",EDGE,"E72.0");var subQ14=sQuery(id+"F12.wireOp",EDGE,"E72.1");var subQ16=sQuery(id+"F12.wireOp",EDGE,"E74.1");var subQ18=sQuery(id+"F12.wireOp",EDGE,"E74.8");Q0=qUnion([makeQuery(id+"F12.imprint","IMPRINT",FACE,{"disambiguationData":[TD([[makeQuery(id+"F12.imprint","IMPRINT",EDGE,{"derivedFrom":subQ7}),1.0]])]}),makeQuery(id+"F12.imprint","IMPRINT",FACE,{"disambiguationData":[TD([[makeQuery(id+"F12.imprint","IMPRINT",EDGE,{"derivedFrom":subQ14}),1.0]])]}),makeQuery(id+"F12.imprint","IMPRINT",FACE,{"disambiguationData":[TD([[makeQuery(id+"F12.imprint","IMPRINT",EDGE,{"derivedFrom":subQ16}),1.0]])]}),makeQuery(id+"F12.imprint","IMPRINT",FACE,{"disambiguationData":[TD([[makeQuery(id+"F12.imprint","IMPRINT",EDGE,{"derivedFrom":subQ18}),-1.0]])]})]);}
            var Q1;
            Q1=makeQuery(id+"F5.boolean.opBoolean","SPLIT",FACE,{"disambiguationData":[TD([makeQuery(id+"F5.opExtrude","SWEPT_FACE",FACE,{"disambiguationData":[OSD([sQuery(id+"F4.wireOp",EDGE,"E41")])]})])],"derivedFrom":makeQuery(id+"F3.boolean.opBoolean","COPY",FACE,{"derivedFrom":makeQuery(id+"F3.opExtrude","CAP_FACE",FACE,{"disambiguationData":[OSD([sQuery(id+"F0.wireOp",EDGE,"E25.0"),sQuery(id+"F0.wireOp",EDGE,"E25.1"),sQuery(id+"F0.wireOp",EDGE,"E25.2"),sQuery(id+"F0.wireOp",EDGE,"E25.3"),sQuery(id+"F0.wireOp",EDGE,"E25.4"),sQuery(id+"F0.wireOp",EDGE,"E25.5"),sQuery(id+"F0.wireOp",EDGE,"E25.6"),sQuery(id+"F0.wireOp",EDGE,"E25.7")])],"isStart":false})})});
            extrude(context, id + "F13", {"entities" : qUnion([Q0]), "operationType" : NewBodyOperationType.REMOVE, "endBound" : BoundingType.UP_TO_SURFACE, "endBoundEntityFace" : qUnion([Q1]), "depth" : 25 * mm});
        }
        {
            var Q0;
            Q0=makeQuery(id+"F3.boolean.opBoolean","COPY",EDGE,{"derivedFrom":makeQuery(id+"F3.opExtrude","CAP_EDGE",EDGE,{"disambiguationData":[OSD([sQuery(id+"F0.wireOp",EDGE,"E25.6")])],"isStart":false})});
            var Q1;
            Q1=makeQuery(id+"F8.boolean.opBoolean","INTERSECT",EDGE,{"derivedFrom":[makeQuery(id+"F5.opExtrude","SWEPT_FACE",FACE,{"disambiguationData":[OSD([sQuery(id+"F4.wireOp",EDGE,"E30")])]}),makeQuery(id+"F8.opExtrude","CAP_FACE",FACE,{"disambiguationData":[OSD([sQuery(id+"F7.wireOp",EDGE,"E67")])],"isStart":false})]});
            var Q2;
            Q2=makeQuery(id+"F8.boolean.opBoolean","INTERSECT",EDGE,{"disambiguationData":[OD(1.0)],"derivedFrom":[makeQuery(id+"F5.opExtrude","SWEPT_FACE",FACE,{"disambiguationData":[OSD([sQuery(id+"F4.wireOp",EDGE,"E30")])]}),makeQuery(id+"F8.opExtrude","SWEPT_FACE",FACE,{"disambiguationData":[OSD([sQuery(id+"F7.wireOp",EDGE,"E67")])]})]});
            var Q3;
            {var subQ0=sQuery(id+"F4.wireOp",EDGE,"E30");Q3=makeQuery(id+"F8.boolean.opBoolean","SPLIT",EDGE,{"disambiguationData":[TD([makeQuery(id+"F5.opExtrude","SWEPT_FACE",FACE,{"disambiguationData":[OSD([sQuery(id+"F4.wireOp",EDGE,"E35.filletArc")])]})])],"derivedFrom":makeQuery(id+"F5.opExtrude","CAP_EDGE",EDGE,{"disambiguationData":[OSD([subQ0])],"isStart":false})});}
            var Q4;
            {var subQ0=sQuery(id+"F0.wireOp",EDGE,"E25.7");var subQ1=sQuery(id+"F0.wireOp",EDGE,"E25.1");var subQ2=sQuery(id+"F0.wireOp",EDGE,"E25.6");var subQ3=sQuery(id+"F0.wireOp",EDGE,"E25.5");var subQ4=sQuery(id+"F0.wireOp",EDGE,"E25.4");var subQ5=sQuery(id+"F0.wireOp",EDGE,"E25.0");var subQ6=sQuery(id+"F0.wireOp",EDGE,"E25.2");var subQ7=sQuery(id+"F0.wireOp",EDGE,"E25.3");Q4=makeQuery(id+"F8.boolean.opBoolean","INTERSECT",EDGE,{"derivedFrom":[makeQuery(id+"F5.boolean.opBoolean","SPLIT",FACE,{"disambiguationData":[TD([makeQuery(id+"F2.opExtrude","SWEPT_FACE",FACE,{"disambiguationData":[OSD([subQ5])]})])],"derivedFrom":makeQuery(id+"F3.boolean.opBoolean","COPY",FACE,{"derivedFrom":makeQuery(id+"F3.opExtrude","CAP_FACE",FACE,{"disambiguationData":[OSD([subQ5,subQ1,subQ6,subQ7,subQ4,subQ3,subQ2,subQ0])],"isStart":false})})}),makeQuery(id+"F8.opExtrude","SWEPT_FACE",FACE,{"disambiguationData":[OSD([sQuery(id+"F7.wireOp",EDGE,"E67")])]})]});}
            var Q5;
            Q5=makeQuery(id+"F8.boolean.opBoolean","INTERSECT",EDGE,{"disambiguationData":[OD(0.0)],"derivedFrom":[makeQuery(id+"F5.opExtrude","SWEPT_FACE",FACE,{"disambiguationData":[OSD([sQuery(id+"F4.wireOp",EDGE,"E30")])]}),makeQuery(id+"F8.opExtrude","SWEPT_FACE",FACE,{"disambiguationData":[OSD([sQuery(id+"F7.wireOp",EDGE,"E67")])]})]});
            fillet(context, id + "F14", {"entities" : qUnion([Q0, Q1, Q2, Q3, Q4, Q5]), "radius" : 3 * mm, "tangentPropagation" : true, "allowEdgeOverflow" : false});
        }
        {
            var Q0;
            Q0=makeQuery(id+"F1.opExtrude","CAP_EDGE",EDGE,{"disambiguationData":[OSD([sQuery(id+"F0.wireOp",EDGE,"E1.bottom")])],"isStart":false});
            fillet(context, id + "F15", {"entities" : qUnion([Q0]), "radius" : 2 * mm, "tangentPropagation" : true, "allowEdgeOverflow" : false});
        }
        {
            var Q0;
            {var subQ0=sQuery(id+"F0.wireOp",EDGE,"E21.filletArc");var subQ1=sQuery(id+"F0.wireOp",EDGE,"E7");var subQ2=sQuery(id+"F0.wireOp",EDGE,"E6");var subQ3=sQuery(id+"F0.wireOp",EDGE,"E5");var subQ4=sQuery(id+"F0.wireOp",EDGE,"E4");var subQ5=sQuery(id+"F0.wireOp",EDGE,"E22.filletArc");var subQ6=sQuery(id+"F0.wireOp",EDGE,"E1.bottom");var subQ7=sQuery(id+"F0.wireOp",EDGE,"E1.right");var subQ8=sQuery(id+"F0.wireOp",EDGE,"E1.top");var subQ9=sQuery(id+"F0.wireOp",EDGE,"E1.left");var subQ10=sQuery(id+"F0.wireOp",EDGE,"E23.filletArc");var subQ11=sQuery(id+"F0.wireOp",EDGE,"E24.filletArc");Q0=makeQuery(id+"F2.boolean.opBoolean","SPLIT",FACE,{"disambiguationData":[TD([makeQuery(id+"F1.opExtrude","SWEPT_FACE",FACE,{"disambiguationData":[OSD([subQ6])]})])],"derivedFrom":makeQuery(id+"F1.opExtrude","CAP_FACE",FACE,{"disambiguationData":[OSD([subQ6,subQ8,subQ9,subQ7,subQ4,subQ3,subQ2,subQ1,subQ0,subQ5,subQ10,subQ11])],"isStart":true})});}
            var sketch = newSketch(context, id + "F16", { "sketchPlane" : qUnion([Q0])});
            skCircle(sketch, "E79", {"center": v(0, 104.25) * mm, "radius": 6 * mm});
            skArc(sketch, "E80", {"start": v(15, 104.25) * mm, "mid": v(0, 119.25) * mm, "end": v(-15, 104.25) * mm});
            skLineSegment(sketch, "E81", {"start": v(-15, 104.25) * mm, "end": v(-15, 92.25) * mm});
            skLineSegment(sketch, "E82", {"start": v(15, 104.25) * mm, "end": v(15, 92.25) * mm});
            skLineSegment(sketch, "E83", {"start": v(-15, 92.25) * mm, "end": v(-33, 74.25) * mm});
            skLineSegment(sketch, "E84", {"start": v(15, 92.25) * mm, "end": v(33, 74.25) * mm});
            skLineSegment(sketch, "E85", {"start": v(0, 74.25) * mm, "end": v(0, 104.25) * mm, "construction": true});
            skLineSegment(sketch, "E86", {"start": v(-74.25, 0) * mm, "end": v(74.25, 0) * mm, "construction": true});
            skLineSegment(sketch, "E87.MirrorCS", {"start": v(-15, -92.25) * mm, "end": v(-33, -74.25) * mm});
            skLineSegment(sketch, "E88.MirrorCS", {"start": v(15, -92.25) * mm, "end": v(33, -74.25) * mm});
            skLineSegment(sketch, "E89.MirrorCS", {"start": v(15, -104.25) * mm, "end": v(15, -92.25) * mm});
            skLineSegment(sketch, "E90.MirrorCS", {"start": v(-15, -104.25) * mm, "end": v(-15, -92.25) * mm});
            skArc(sketch, "E91.MirrorCS", {"start": v(15, -104.25) * mm, "mid": v(0, -119.25) * mm, "end": v(-15, -104.25) * mm});
            skCircle(sketch, "E92.MirrorC", {"center": v(0, -104.25) * mm, "radius": 6 * mm});
            skSolve(sketch);
        }
        {
            var Q0;
            Q0=makeQuery(id+"F16.imprint","IMPRINT",FACE,{"disambiguationData":[TD([[makeQuery(id+"F16.imprint","IMPRINT",EDGE,{"derivedFrom":makeQuery(id+"F1.opExtrude","CAP_EDGE",EDGE,{"disambiguationData":[OSD([sQuery(id+"F0.wireOp",EDGE,"E1.left")])],"isStart":true})}),-1.0]])]});
            var Q1;
            {var subQ1=sQuery(id+"F16.wireOp",EDGE,"E87.MirrorCS");Q1=makeQuery(id+"F16.imprint","IMPRINT",FACE,{"disambiguationData":[TD([[makeQuery(id+"F16.imprint","IMPRINT",EDGE,{"derivedFrom":subQ1}),-1.0]])]});}
            var Q2;
            Q2=makeQuery(id+"F16.imprint","IMPRINT",FACE,{"disambiguationData":[TD([[makeQuery(id+"F16.imprint","IMPRINT",EDGE,{"derivedFrom":sQuery(id+"F16.wireOp",EDGE,"E79")}),-1.0]])]});
            var Q3;
            Q3=makeQuery(id+"F2.opExtrude","CAP_FACE",FACE,{"disambiguationData":[OSD([sQuery(id+"F0.wireOp",EDGE,"E12"),sQuery(id+"F0.wireOp",EDGE,"E13"),sQuery(id+"F0.wireOp",EDGE,"E14"),sQuery(id+"F0.wireOp",EDGE,"E15"),sQuery(id+"F0.wireOp",EDGE,"E17.filletArc"),sQuery(id+"F0.wireOp",EDGE,"E18.filletArc"),sQuery(id+"F0.wireOp",EDGE,"E19.filletArc"),sQuery(id+"F0.wireOp",EDGE,"E20.filletArc"),sQuery(id+"F0.wireOp",EDGE,"E25.0"),sQuery(id+"F0.wireOp",EDGE,"E25.1"),sQuery(id+"F0.wireOp",EDGE,"E25.2"),sQuery(id+"F0.wireOp",EDGE,"E25.3"),sQuery(id+"F0.wireOp",EDGE,"E25.4"),sQuery(id+"F0.wireOp",EDGE,"E25.5"),sQuery(id+"F0.wireOp",EDGE,"E25.6"),sQuery(id+"F0.wireOp",EDGE,"E25.7")])],"isStart":false});
            extrude(context, id + "F17", {"entities" : qUnion([Q0, Q1, Q2]), "endBound" : BoundingType.UP_TO_SURFACE, "endBoundEntityFace" : qUnion([Q3]), "depth" : 25 * mm});
        }
    });
